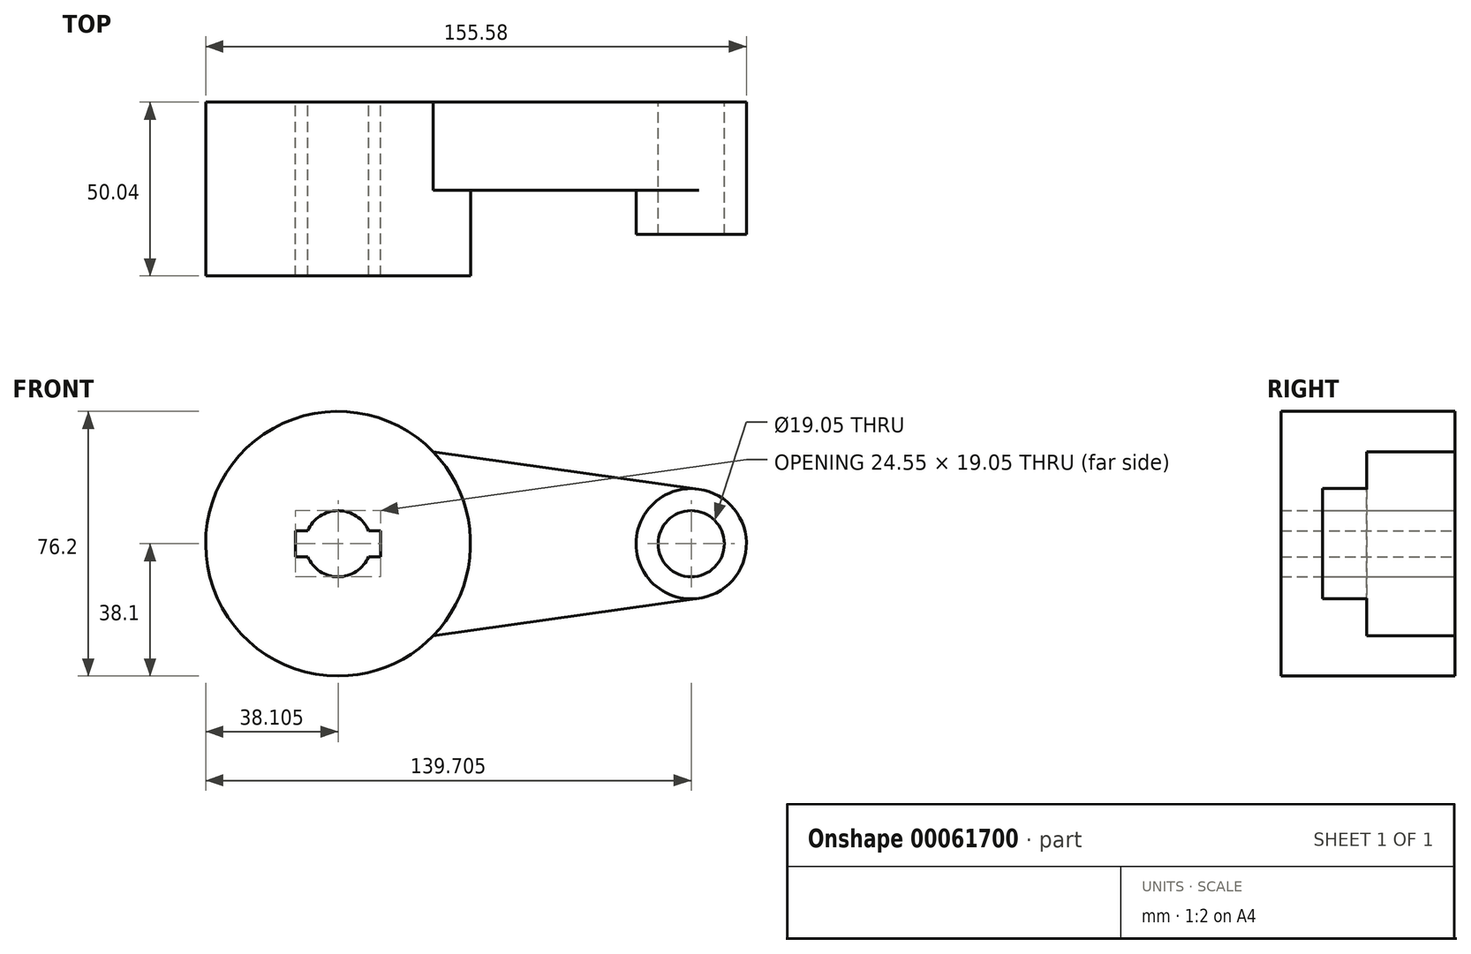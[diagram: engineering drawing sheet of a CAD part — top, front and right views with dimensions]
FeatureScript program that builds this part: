
annotation { "Feature Type Name" : "Feature", "Feature Type Description" : "" }
export const myFeature = defineFeature(function(context is Context, id is Id, definition is map)
    precondition{}
    {
        {
            var Q0;
            Q0=qCreatedBy(makeId("Front.planeOp"),FACE);
            var sketch = newSketch(context, id + "F0", { "sketchPlane" : qUnion([Q0])});
            skCircle(sketch, "E0", {"center": v(-56.28, 0) * mm, "radius": 38.1 * mm});
            skCircle(sketch, "E1", {"center": v(45.32, 0) * mm, "radius": 15.88 * mm});
            skLineSegment(sketch, "E2", {"start": v(-28.86, 26.46) * mm, "end": v(47.53, 15.72) * mm});
            skLineSegment(sketch, "E3", {"start": v(-28.86, -26.46) * mm, "end": v(47.53, -15.72) * mm});
            skCircle(sketch, "E4", {"center": v(-56.28, 0) * mm, "radius": 9.53 * mm});
            skCircle(sketch, "E5", {"center": v(45.32, 0) * mm, "radius": 9.53 * mm});
            skLineSegment(sketch, "E6.rect.bottom", {"start": v(-44, -3.7) * mm, "end": v(-68.55, -3.7) * mm});
            skLineSegment(sketch, "E6.rect.top", {"start": v(-44, 3.7) * mm, "end": v(-68.55, 3.7) * mm});
            skLineSegment(sketch, "E6.rect.left", {"start": v(-44, -3.7) * mm, "end": v(-44, 3.7) * mm});
            skLineSegment(sketch, "E6.rect.right", {"start": v(-68.55, -3.7) * mm, "end": v(-68.55, 3.7) * mm});
            skSolve(sketch);
        }
        {
            var Q0;
            {var subQ0=sQuery(id+"F0.wireOp",EDGE,"E2");Q0=makeQuery(id+"F0.imprint","IMPRINT",FACE,{"disambiguationData":[TD([[makeQuery(id+"F0.imprint","IMPRINT",EDGE,{"derivedFrom":subQ0}),-1.0]])]});}
            var Q1;
            Q1=makeQuery(id+"F0.imprint","IMPRINT",FACE,{"disambiguationData":[TD([[makeQuery(id+"F0.imprint","IMPRINT",EDGE,{"derivedFrom":sQuery(id+"F0.wireOp",EDGE,"E5")}),-1.0]])]});
            var Q2;
            {var subQ11=sQuery(id+"F0.wireOp",EDGE,"E6.rect.left");Q2=makeQuery(id+"F0.imprint","IMPRINT",FACE,{"disambiguationData":[TD([[makeQuery(id+"F0.imprint","IMPRINT",EDGE,{"derivedFrom":subQ11}),-1.0]])]});}
            extrude(context, id + "F1", {"entities" : qUnion([Q0, Q1, Q2]), "depth" : 25.4 * mm});
        }
        {
            var Q0;
            {var subQ11=sQuery(id+"F0.wireOp",EDGE,"E6.rect.left");Q0=makeQuery(id+"F0.imprint","IMPRINT",FACE,{"disambiguationData":[TD([[makeQuery(id+"F0.imprint","IMPRINT",EDGE,{"derivedFrom":subQ11}),-1.0]])]});}
            extrude(context, id + "F2", {"entities" : qUnion([Q0]), "operationType" : NewBodyOperationType.ADD, "depth" : 50.04 * mm});
        }
        {
            var Q0;
            Q0=makeQuery(id+"F0.imprint","IMPRINT",FACE,{"disambiguationData":[TD([[makeQuery(id+"F0.imprint","IMPRINT",EDGE,{"derivedFrom":sQuery(id+"F0.wireOp",EDGE,"E5")}),-1.0]])]});
            extrude(context, id + "F3", {"entities" : qUnion([Q0]), "operationType" : NewBodyOperationType.ADD, "depth" : 38.1 * mm});
        }
    });
